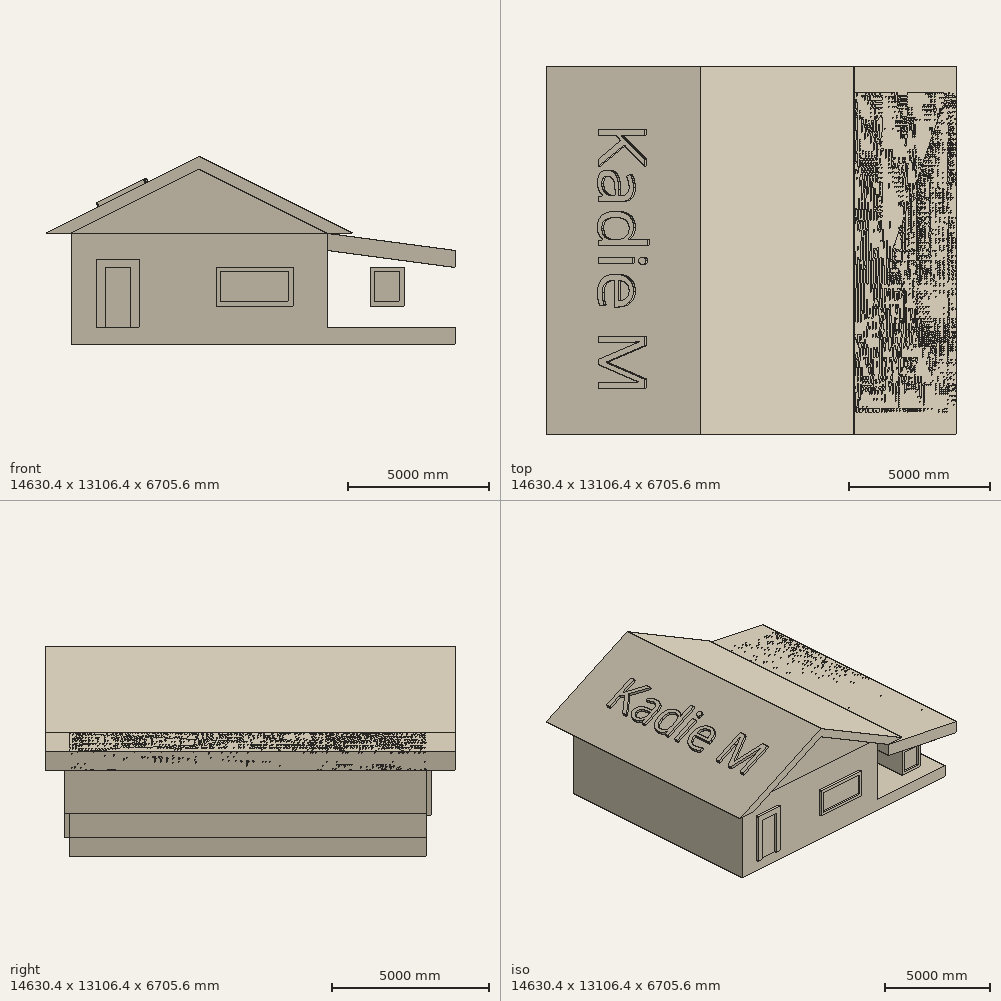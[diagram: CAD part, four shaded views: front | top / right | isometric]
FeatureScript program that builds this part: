
annotation { "Feature Type Name" : "Feature", "Feature Type Description" : "" }
export const myFeature = defineFeature(function(context is Context, id is Id, definition is map)
    precondition{}
    {
        {
            var Q0;
            Q0=qCreatedBy(makeId("Front.planeOp"),FACE);
            var sketch = newSketch(context, id + "F0", { "sketchPlane" : qUnion([Q0])});
            skLineSegment(sketch, "E0", {"start": v(0, 0) * mm, "end": v(4572, 0) * mm});
            skLineSegment(sketch, "E1", {"start": v(0, 0) * mm, "end": v(-4572, 0) * mm});
            skLineSegment(sketch, "E2", {"start": v(0, 0) * mm, "end": v(0, 2286) * mm});
            skLineSegment(sketch, "E3", {"start": v(-4572, 0) * mm, "end": v(0, 2286) * mm});
            skLineSegment(sketch, "E4", {"start": v(0, 2286) * mm, "end": v(4572, 0) * mm});
            skLineSegment(sketch, "E5", {"start": v(0, 2286) * mm, "end": v(0, 2743.2) * mm});
            skLineSegment(sketch, "E6", {"start": v(-4572, 0) * mm, "end": v(-5486.4, 0) * mm});
            skLineSegment(sketch, "E7", {"start": v(4572, 0) * mm, "end": v(5486.4, 0) * mm});
            skLineSegment(sketch, "E8", {"start": v(0, 2743.2) * mm, "end": v(-5486.4, 0) * mm});
            skLineSegment(sketch, "E9", {"start": v(0, 2743.2) * mm, "end": v(5486.4, 0) * mm});
            skLineSegment(sketch, "E10", {"start": v(-4572, 0) * mm, "end": v(-4572, -3352.8) * mm});
            skLineSegment(sketch, "E11", {"start": v(4572, 0) * mm, "end": v(4572, -3352.8) * mm});
            skLineSegment(sketch, "E12", {"start": v(4572, -3352.8) * mm, "end": v(-4572, -3352.8) * mm});
            skLineSegment(sketch, "E13", {"start": v(4572, -3352.8) * mm, "end": v(4572, -3962.4) * mm});
            skLineSegment(sketch, "E14", {"start": v(-4572, -3352.8) * mm, "end": v(-4572, -3962.4) * mm});
            skLineSegment(sketch, "E15", {"start": v(-4572, -3962.4) * mm, "end": v(4572, -3962.4) * mm});
            skLineSegment(sketch, "E16", {"start": v(4572, -3962.4) * mm, "end": v(9144, -3962.4) * mm});
            skLineSegment(sketch, "E17", {"start": v(9144, -3962.4) * mm, "end": v(9144, -3352.8) * mm});
            skLineSegment(sketch, "E18", {"start": v(9144, -3352.8) * mm, "end": v(9144, -609.6) * mm});
            skLineSegment(sketch, "E19", {"start": v(9144, -609.6) * mm, "end": v(4572, 0) * mm});
            skLineSegment(sketch, "E20", {"start": v(4572, 0) * mm, "end": v(4572, -609.6) * mm});
            skLineSegment(sketch, "E21", {"start": v(4572, -3352.8) * mm, "end": v(9144, -3352.8) * mm});
            skLineSegment(sketch, "E22", {"start": v(9144, -609.6) * mm, "end": v(9144, -1219.2) * mm});
            skLineSegment(sketch, "E23", {"start": v(9144, -1219.2) * mm, "end": v(4572, -609.6) * mm});
            skLineSegment(sketch, "E24.bottom", {"start": v(6096, -1219.2) * mm, "end": v(7315.2, -1219.2) * mm});
            skLineSegment(sketch, "E24.top", {"start": v(6096, -2590.8) * mm, "end": v(7315.2, -2590.8) * mm});
            skLineSegment(sketch, "E24.left", {"start": v(6096, -1219.2) * mm, "end": v(6096, -2590.8) * mm});
            skLineSegment(sketch, "E24.right", {"start": v(7315.2, -1219.2) * mm, "end": v(7315.2, -2590.8) * mm});
            skLineSegment(sketch, "E25.0", {"start": v(6248.4, -1371.6) * mm, "end": v(7162.8, -1371.6) * mm});
            skLineSegment(sketch, "E25.1", {"start": v(6248.4, -1371.6) * mm, "end": v(6248.4, -2438.4) * mm});
            skLineSegment(sketch, "E25.2", {"start": v(6248.4, -2438.4) * mm, "end": v(7162.8, -2438.4) * mm});
            skLineSegment(sketch, "E25.3", {"start": v(7162.8, -1371.6) * mm, "end": v(7162.8, -2438.4) * mm});
            skLineSegment(sketch, "E26", {"start": v(-3352.8, -3352.8) * mm, "end": v(-3352.8, -1219.2) * mm});
            skLineSegment(sketch, "E27", {"start": v(-3352.8, -1219.2) * mm, "end": v(-2438.4, -1219.2) * mm});
            skLineSegment(sketch, "E28", {"start": v(-2438.4, -1219.2) * mm, "end": v(-2438.4, -3352.8) * mm});
            skLineSegment(sketch, "E29", {"start": v(-2438.4, -3352.8) * mm, "end": v(-3352.8, -3352.8) * mm});
            skLineSegment(sketch, "E30.0", {"start": v(-2133.6, -914.4) * mm, "end": v(-2133.6, -3352.8) * mm});
            skLineSegment(sketch, "E30.1", {"start": v(-3657.6, -914.4) * mm, "end": v(-2133.6, -914.4) * mm});
            skLineSegment(sketch, "E30.2", {"start": v(-3657.6, -3352.8) * mm, "end": v(-3657.6, -914.4) * mm});
            skLineSegment(sketch, "E31.bottom", {"start": v(609.6, -1219.2) * mm, "end": v(3352.8, -1219.2) * mm});
            skLineSegment(sketch, "E31.top", {"start": v(609.6, -2590.8) * mm, "end": v(3352.8, -2590.8) * mm});
            skLineSegment(sketch, "E31.left", {"start": v(609.6, -1219.2) * mm, "end": v(609.6, -2590.8) * mm});
            skLineSegment(sketch, "E31.right", {"start": v(3352.8, -1219.2) * mm, "end": v(3352.8, -2590.8) * mm});
            skLineSegment(sketch, "E32.0", {"start": v(762, -1371.6) * mm, "end": v(3200.4, -1371.6) * mm});
            skLineSegment(sketch, "E32.1", {"start": v(762, -1371.6) * mm, "end": v(762, -2438.4) * mm});
            skLineSegment(sketch, "E32.2", {"start": v(762, -2438.4) * mm, "end": v(3200.4, -2438.4) * mm});
            skLineSegment(sketch, "E32.3", {"start": v(3200.4, -1371.6) * mm, "end": v(3200.4, -2438.4) * mm});
            skText(sketch, "E33", { "text": "Kadie M", "fontName": "OpenSans-Bold.ttf"});
            const initialGuessF0  = {"E33": [3.4121, 1.32891, 1, 0, 0.50257]};
            skSetInitialGuess(sketch, initialGuessF0);
            skSolve(sketch);
        }
        {
            var Q0;
            Q0=makeQuery(id+"F0.imprint","IMPRINT",FACE,{"disambiguationData":[TD([[makeQuery(id+"F0.imprint","IMPRINT",EDGE,{"derivedFrom":sQuery(id+"F0.wireOp",EDGE,"E3")}),1.0]])]});
            var Q1;
            Q1=makeQuery(id+"F0.imprint","IMPRINT",FACE,{"disambiguationData":[TD([[makeQuery(id+"F0.imprint","IMPRINT",EDGE,{"derivedFrom":sQuery(id+"F0.wireOp",EDGE,"E4")}),1.0]])]});
            var Q2;
            Q2=makeQuery(id+"F0.imprint","IMPRINT",FACE,{"disambiguationData":[TD([[makeQuery(id+"F0.imprint","IMPRINT",EDGE,{"derivedFrom":sQuery(id+"F0.wireOp",EDGE,"E19")}),1.0]])]});
            extrude(context, id + "F1", {"entities" : qUnion([Q0, Q1, Q2]), "depth" : 914.4 * mm, "offsetDistance" : 30.48 * mm, "hasSecondDirection" : true, "secondDirectionOppositeDirection" : true, "secondDirectionDepth" : 12192 * mm});
        }
        {
            var Q0;
            Q0=makeQuery(id+"F0.imprint","IMPRINT",FACE,{"disambiguationData":[TD([[makeQuery(id+"F0.imprint","IMPRINT",EDGE,{"derivedFrom":sQuery(id+"F0.wireOp",EDGE,"E1")}),-1.0]])]});
            var Q1;
            Q1=makeQuery(id+"F0.imprint","IMPRINT",FACE,{"disambiguationData":[TD([[makeQuery(id+"F0.imprint","IMPRINT",EDGE,{"derivedFrom":sQuery(id+"F0.wireOp",EDGE,"E0")}),1.0]])]});
            extrude(context, id + "F2", {"entities" : qUnion([Q0, Q1]), "operationType" : NewBodyOperationType.ADD, "depth" : 152.4 * mm, "offsetDistance" : 30.48 * mm, "hasSecondDirection" : true, "secondDirectionOppositeDirection" : true, "secondDirectionDepth" : 11277.6 * mm});
        }
        {
            var Q0;
            Q0=makeQuery(id+"F0.imprint","IMPRINT",FACE,{"disambiguationData":[TD([[makeQuery(id+"F0.imprint","IMPRINT",EDGE,{"derivedFrom":sQuery(id+"F0.wireOp",EDGE,"E0")}),-1.0]])]});
            var Q1;
            {var subQ1=sQuery(id+"F0.wireOp",EDGE,"E26");Q1=makeQuery(id+"F0.imprint","IMPRINT",FACE,{"disambiguationData":[TD([[makeQuery(id+"F0.imprint","IMPRINT",EDGE,{"derivedFrom":subQ1}),1.0]])]});}
            var Q2;
            Q2=makeQuery(id+"F0.imprint","IMPRINT",FACE,{"disambiguationData":[TD([[makeQuery(id+"F0.imprint","IMPRINT",EDGE,{"derivedFrom":sQuery(id+"F0.wireOp",EDGE,"E26")}),-1.0]])]});
            var Q3;
            Q3=makeQuery(id+"F0.imprint","IMPRINT",FACE,{"disambiguationData":[TD([[makeQuery(id+"F0.imprint","IMPRINT",EDGE,{"derivedFrom":sQuery(id+"F0.wireOp",EDGE,"E32.0")}),-1.0]])]});
            var Q4;
            Q4=makeQuery(id+"F0.imprint","IMPRINT",FACE,{"disambiguationData":[TD([[makeQuery(id+"F0.imprint","IMPRINT",EDGE,{"derivedFrom":sQuery(id+"F0.wireOp",EDGE,"E25.0")}),-1.0]])]});
            var Q5;
            Q5=makeQuery(id+"F0.imprint","IMPRINT",FACE,{"disambiguationData":[TD([[makeQuery(id+"F0.imprint","IMPRINT",EDGE,{"derivedFrom":sQuery(id+"F0.wireOp",EDGE,"E11")}),1.0]])]});
            var Q6;
            Q6=makeQuery(id+"F0.imprint","IMPRINT",FACE,{"disambiguationData":[TD([[makeQuery(id+"F0.imprint","IMPRINT",EDGE,{"derivedFrom":sQuery(id+"F0.wireOp",EDGE,"E13")}),1.0]])]});
            var Q7;
            {var subQ5=sQuery(id+"F0.wireOp",EDGE,"E13");Q7=makeQuery(id+"F0.imprint","IMPRINT",FACE,{"disambiguationData":[TD([[makeQuery(id+"F0.imprint","IMPRINT",EDGE,{"derivedFrom":subQ5}),-1.0]])]});}
            var Q8;
            Q8=makeQuery(id+"F0.imprint","IMPRINT",FACE,{"disambiguationData":[TD([[makeQuery(id+"F0.imprint","IMPRINT",EDGE,{"derivedFrom":sQuery(id+"F0.wireOp",EDGE,"E31.bottom")}),-1.0]])]});
            var Q9;
            Q9=makeQuery(id+"F0.imprint","IMPRINT",FACE,{"disambiguationData":[TD([[makeQuery(id+"F0.imprint","IMPRINT",EDGE,{"derivedFrom":sQuery(id+"F0.wireOp",EDGE,"E24.bottom")}),-1.0]])]});
            extrude(context, id + "F3", {"entities" : qUnion([Q0, Q1, Q2, Q3, Q4, Q5, Q6, Q7, Q8, Q9]), "depth" : 152.4 * mm, "offsetDistance" : 30.48 * mm, "hasSecondDirection" : true, "secondDirectionOppositeDirection" : true, "secondDirectionDepth" : 11277.6 * mm});
        }
        {
            var Q0;
            Q0=makeQuery(id+"F3.opExtrude","CAP_FACE",FACE,{"disambiguationData":[OSD([sQuery(id+"F0.wireOp",EDGE,"E0"),sQuery(id+"F0.wireOp",EDGE,"E1"),sQuery(id+"F0.wireOp",EDGE,"E10"),sQuery(id+"F0.wireOp",EDGE,"E14"),sQuery(id+"F0.wireOp",EDGE,"E15"),sQuery(id+"F0.wireOp",EDGE,"E16"),sQuery(id+"F0.wireOp",EDGE,"E17"),sQuery(id+"F0.wireOp",EDGE,"E18"),sQuery(id+"F0.wireOp",EDGE,"E20"),sQuery(id+"F0.wireOp",EDGE,"E23")])],"isStart":false});
            var sketch = newSketch(context, id + "F4", { "sketchPlane" : qUnion([Q0])});
            skLineSegment(sketch, "E34.bottom", {"start": v(609.6, -1219.2) * mm, "end": v(3352.8, -1219.2) * mm});
            skLineSegment(sketch, "E34.top", {"start": v(609.6, -2590.8) * mm, "end": v(3352.8, -2590.8) * mm});
            skLineSegment(sketch, "E34.left", {"start": v(609.6, -1219.2) * mm, "end": v(609.6, -2590.8) * mm});
            skLineSegment(sketch, "E34.right", {"start": v(3352.8, -1219.2) * mm, "end": v(3352.8, -2590.8) * mm});
            skLineSegment(sketch, "E35.0", {"start": v(762, -1371.6) * mm, "end": v(3200.4, -1371.6) * mm});
            skLineSegment(sketch, "E35.1", {"start": v(762, -1371.6) * mm, "end": v(762, -2438.4) * mm});
            skLineSegment(sketch, "E35.2", {"start": v(762, -2438.4) * mm, "end": v(3200.4, -2438.4) * mm});
            skLineSegment(sketch, "E35.3", {"start": v(3200.4, -1371.6) * mm, "end": v(3200.4, -2438.4) * mm});
            skLineSegment(sketch, "E36.bottom", {"start": v(-3352.8, -1219.2) * mm, "end": v(-2438.4, -1219.2) * mm});
            skLineSegment(sketch, "E36.top", {"start": v(-3352.8, -3352.8) * mm, "end": v(-2438.4, -3352.8) * mm});
            skLineSegment(sketch, "E36.left", {"start": v(-3352.8, -1219.2) * mm, "end": v(-3352.8, -3352.8) * mm});
            skLineSegment(sketch, "E36.right", {"start": v(-2438.4, -1219.2) * mm, "end": v(-2438.4, -3352.8) * mm});
            skLineSegment(sketch, "E37.bottom", {"start": v(6096, -1219.2) * mm, "end": v(7315.2, -1219.2) * mm});
            skLineSegment(sketch, "E37.top", {"start": v(6096, -2590.8) * mm, "end": v(7315.2, -2590.8) * mm});
            skLineSegment(sketch, "E37.left", {"start": v(6096, -1219.2) * mm, "end": v(6096, -2590.8) * mm});
            skLineSegment(sketch, "E37.right", {"start": v(7315.2, -1219.2) * mm, "end": v(7315.2, -2590.8) * mm});
            skLineSegment(sketch, "E38.0", {"start": v(-2133.6, -914.4) * mm, "end": v(-2133.6, -3352.8) * mm});
            skLineSegment(sketch, "E38.1", {"start": v(-3657.6, -914.4) * mm, "end": v(-2133.6, -914.4) * mm});
            skLineSegment(sketch, "E38.2", {"start": v(-3657.6, -914.4) * mm, "end": v(-3657.6, -3352.8) * mm});
            skLineSegment(sketch, "E39.0", {"start": v(7162.8, -1371.6) * mm, "end": v(7162.8, -2438.4) * mm});
            skLineSegment(sketch, "E39.1", {"start": v(6248.4, -1371.6) * mm, "end": v(7162.8, -1371.6) * mm});
            skLineSegment(sketch, "E39.2", {"start": v(6248.4, -1371.6) * mm, "end": v(6248.4, -2438.4) * mm});
            skLineSegment(sketch, "E39.3", {"start": v(6248.4, -2438.4) * mm, "end": v(7162.8, -2438.4) * mm});
            skLineSegment(sketch, "E40", {"start": v(-2133.6, -3352.8) * mm, "end": v(-3657.6, -3352.8) * mm});
            skSolve(sketch);
        }
        {
            var Q0;
            Q0=makeQuery(id+"F4.imprint","IMPRINT",FACE,{"disambiguationData":[TD([[makeQuery(id+"F4.imprint","IMPRINT",EDGE,{"derivedFrom":sQuery(id+"F4.wireOp",EDGE,"E36.bottom")}),-1.0]])]});
            var Q1;
            Q1=makeQuery(id+"F4.imprint","IMPRINT",FACE,{"disambiguationData":[TD([[makeQuery(id+"F4.imprint","IMPRINT",EDGE,{"derivedFrom":sQuery(id+"F4.wireOp",EDGE,"E35.0")}),-1.0]])]});
            var Q2;
            Q2=makeQuery(id+"F4.imprint","IMPRINT",FACE,{"disambiguationData":[TD([[makeQuery(id+"F4.imprint","IMPRINT",EDGE,{"derivedFrom":sQuery(id+"F4.wireOp",EDGE,"E39.0")}),-1.0]])]});
            extrude(context, id + "F5", {"entities" : qUnion([Q0, Q1, Q2]), "operationType" : NewBodyOperationType.ADD, "depth" : 60.96 * mm, "offsetDistance" : 30.48 * mm, "hasSecondDirection" : true, "secondDirectionOppositeDirection" : true, "secondDirectionDepth" : 60.96 * mm});
        }
        {
            var Q0;
            Q0=makeQuery(id+"F4.imprint","IMPRINT",FACE,{"disambiguationData":[TD([[makeQuery(id+"F4.imprint","IMPRINT",EDGE,{"derivedFrom":sQuery(id+"F4.wireOp",EDGE,"E37.bottom")}),-1.0]])]});
            var Q1;
            Q1=makeQuery(id+"F4.imprint","IMPRINT",FACE,{"disambiguationData":[TD([[makeQuery(id+"F4.imprint","IMPRINT",EDGE,{"derivedFrom":sQuery(id+"F4.wireOp",EDGE,"E34.bottom")}),-1.0]])]});
            extrude(context, id + "F6", {"entities" : qUnion([Q0, Q1]), "operationType" : NewBodyOperationType.ADD, "depth" : 152.4 * mm, "offsetDistance" : 30.48 * mm, "hasSecondDirection" : true, "secondDirectionOppositeDirection" : true, "secondDirectionDepth" : 152.4 * mm});
        }
        {
            var Q0;
            Q0=makeQuery(id+"F4.imprint","IMPRINT",FACE,{"disambiguationData":[TD([[makeQuery(id+"F4.imprint","IMPRINT",EDGE,{"derivedFrom":sQuery(id+"F4.wireOp",EDGE,"E36.bottom")}),1.0]])]});
            extrude(context, id + "F7", {"entities" : qUnion([Q0]), "operationType" : NewBodyOperationType.ADD, "depth" : 152.4 * mm, "offsetDistance" : 30.48 * mm, "hasSecondDirection" : true, "secondDirectionOppositeDirection" : true, "secondDirectionDepth" : 152.4 * mm});
        }
        {
            var Q0;
            Q0=makeQuery(id+"F3.opExtrude","CAP_FACE",FACE,{"disambiguationData":[OSD([sQuery(id+"F0.wireOp",EDGE,"E0"),sQuery(id+"F0.wireOp",EDGE,"E1"),sQuery(id+"F0.wireOp",EDGE,"E10"),sQuery(id+"F0.wireOp",EDGE,"E14"),sQuery(id+"F0.wireOp",EDGE,"E15"),sQuery(id+"F0.wireOp",EDGE,"E16"),sQuery(id+"F0.wireOp",EDGE,"E17"),sQuery(id+"F0.wireOp",EDGE,"E18"),sQuery(id+"F0.wireOp",EDGE,"E20"),sQuery(id+"F0.wireOp",EDGE,"E23")])],"isStart":true});
            var sketch = newSketch(context, id + "F8", { "sketchPlane" : qUnion([Q0])});
            skLineSegment(sketch, "E41.bottom", {"start": v(-3048, -685.8) * mm, "end": v(3048, -685.8) * mm});
            skLineSegment(sketch, "E41.top", {"start": v(-3048, -2667) * mm, "end": v(3048, -2667) * mm});
            skLineSegment(sketch, "E41.left", {"start": v(-3048, -685.8) * mm, "end": v(-3048, -2667) * mm});
            skLineSegment(sketch, "E41.right", {"start": v(3048, -685.8) * mm, "end": v(3048, -2667) * mm});
            skLineSegment(sketch, "E42.0", {"start": v(-2743.2, -990.6) * mm, "end": v(2743.2, -990.6) * mm});
            skLineSegment(sketch, "E42.1", {"start": v(-2743.2, -990.6) * mm, "end": v(-2743.2, -2362.2) * mm});
            skLineSegment(sketch, "E42.2", {"start": v(-2743.2, -2362.2) * mm, "end": v(2743.2, -2362.2) * mm});
            skLineSegment(sketch, "E42.3", {"start": v(2743.2, -990.6) * mm, "end": v(2743.2, -2362.2) * mm});
            skSolve(sketch);
        }
        {
            var Q0;
            Q0=makeQuery(id+"F8.imprint","IMPRINT",FACE,{"disambiguationData":[TD([[makeQuery(id+"F8.imprint","IMPRINT",EDGE,{"derivedFrom":sQuery(id+"F8.wireOp",EDGE,"E42.0")}),-1.0]])]});
            extrude(context, id + "F9", {"entities" : qUnion([Q0]), "operationType" : NewBodyOperationType.ADD, "depth" : 60.96 * mm, "offsetDistance" : 30.48 * mm, "hasSecondDirection" : true, "secondDirectionOppositeDirection" : true, "secondDirectionDepth" : 60.96 * mm});
        }
        {
            var Q0;
            Q0=makeQuery(id+"F8.imprint","IMPRINT",FACE,{"disambiguationData":[TD([[makeQuery(id+"F8.imprint","IMPRINT",EDGE,{"derivedFrom":sQuery(id+"F8.wireOp",EDGE,"E41.bottom")}),-1.0]])]});
            extrude(context, id + "F10", {"entities" : qUnion([Q0]), "operationType" : NewBodyOperationType.ADD, "depth" : 152.4 * mm, "offsetDistance" : 30.48 * mm, "hasSecondDirection" : true, "secondDirectionOppositeDirection" : true, "secondDirectionDepth" : 152.4 * mm});
        }
        {
            var Q0;
            Q0=makeQuery(id+"F1.opExtrude","SWEPT_FACE",FACE,{"disambiguationData":[OSD([sQuery(id+"F0.wireOp",EDGE,"E8")])]});
            var sketch = newSketch(context, id + "F11", { "sketchPlane" : qUnion([Q0])});
            skText(sketch, "E43", { "text": "Kadie M", "fontName": "OpenSans-Regular.ttf"});
            const initialGuessF11  = {"E43": [-2.77117, 10.2108, 0, -1, 1.86437]};
            skSetInitialGuess(sketch, initialGuessF11);
            skSolve(sketch);
        }
        {
            var Q0;
            Q0=makeQuery(id+"F11.imprint","IMPRINT",FACE,{"disambiguationData":[TD([[makeQuery(id+"F11.imprint","IMPRINT",EDGE,{"derivedFrom":sQuery(id+"F11.wireOp",EDGE,"E43.sketch_text.stroke-0")}),-1.0]])]});
            var Q1;
            Q1=makeQuery(id+"F11.imprint","IMPRINT",FACE,{"disambiguationData":[TD([[makeQuery(id+"F11.imprint","IMPRINT",EDGE,{"derivedFrom":sQuery(id+"F11.wireOp",EDGE,"E43.sketch_text.stroke-12")}),-1.0]])]});
            var Q2;
            Q2=makeQuery(id+"F11.imprint","IMPRINT",FACE,{"disambiguationData":[TD([[makeQuery(id+"F11.imprint","IMPRINT",EDGE,{"derivedFrom":sQuery(id+"F11.wireOp",EDGE,"E43.sketch_text.stroke-39")}),-1.0]])]});
            var Q3;
            Q3=makeQuery(id+"F11.imprint","IMPRINT",FACE,{"disambiguationData":[TD([[makeQuery(id+"F11.imprint","IMPRINT",EDGE,{"derivedFrom":sQuery(id+"F11.wireOp",EDGE,"E43.sketch_text.stroke-63")}),-1.0]])]});
            var Q4;
            Q4=makeQuery(id+"F11.imprint","IMPRINT",FACE,{"disambiguationData":[TD([[makeQuery(id+"F11.imprint","IMPRINT",EDGE,{"derivedFrom":sQuery(id+"F11.wireOp",EDGE,"E43.sketch_text.stroke-67")}),-1.0]])]});
            var Q5;
            Q5=makeQuery(id+"F11.imprint","IMPRINT",FACE,{"disambiguationData":[TD([[makeQuery(id+"F11.imprint","IMPRINT",EDGE,{"derivedFrom":sQuery(id+"F11.wireOp",EDGE,"E43.sketch_text.stroke-75")}),-1.0]])]});
            extrude(context, id + "F12", {"entities" : qUnion([Q0, Q1, Q2, Q3, Q4, Q5]), "operationType" : NewBodyOperationType.ADD, "depth" : 152.4 * mm, "offsetDistance" : 30.48 * mm, "hasSecondDirection" : true, "secondDirectionOppositeDirection" : true, "secondDirectionDepth" : 152.4 * mm});
        }
        {
            var Q0;
            Q0=makeQuery(id+"F11.imprint","IMPRINT",FACE,{"disambiguationData":[TD([[makeQuery(id+"F11.imprint","IMPRINT",EDGE,{"derivedFrom":sQuery(id+"F11.wireOp",EDGE,"E43.sketch_text.stroke-94")}),-1.0]])]});
            extrude(context, id + "F13", {"entities" : qUnion([Q0]), "operationType" : NewBodyOperationType.ADD, "depth" : 152.4 * mm, "offsetDistance" : 30.48 * mm, "hasSecondDirection" : true, "secondDirectionOppositeDirection" : true, "secondDirectionDepth" : 152.4 * mm});
        }
    });
